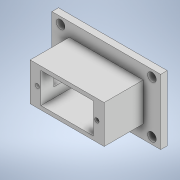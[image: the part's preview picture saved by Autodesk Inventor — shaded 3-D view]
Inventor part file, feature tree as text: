
AUTODESK INVENTOR PART (.ipt)
format: ipt  version: 2020 (Build 240168000, 168)  size: 336,896 bytes
history: native  units: mm
features: sketch x9, extrude x6
ambient origin geometry x8: Origin, YZ Plane, XZ Plane, XY Plane, X Axis, Y Axis, Z Axis, Center Point
bodies: Solid1 (feature_tree)
feature tree (15):
  sketch  "Sketch1"  dims[d0=30.0mm d1=50.0mm]
  extrude  "Extrusion1"  Depth=50.0mm
  extrude  "Extrusion2"  Depth=24.2mm
  extrude  "Extrusion3"  Depth=34.0mm
  extrude  "Extrusion4"  Depth=18.0mm TaperAngle=0.0deg
  sketch  "Sketch7"  dims[d12=10.0mm d13=18.0mm d14=0.0mm]
  extrude  "Extrusion5"  Depth=5.0mm
  sketch  "Sketch9"  dims[d16=2.0mm]
  extrude  "Extrusion6"  Depth=18.0mm TaperAngle=0.0deg
  sketch  "Sketch2"  dims[d2=3.0mm d3=0.0mm d4=24.2mm]
  sketch  "Sketch3"  dims[d5=14.0mm d6=34.0mm]
  sketch  "Sketch5"  dims[d7=17.5mm d8=18.0mm d9=0.0mm]
  sketch  "Sketch6"  dims[d10=14.0mm d11=5.0mm]
  sketch  "Sketch8"  dims[d15=1.6mm]
  sketch  "Sketch10"  dims[d17=5.0mm d18=0.0mm d19=4.0mm d20=3.0mm d21=0.0mm d22=10.0mm d23=0.0mm d24=7.0mm]
